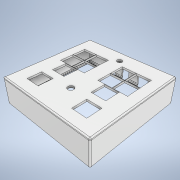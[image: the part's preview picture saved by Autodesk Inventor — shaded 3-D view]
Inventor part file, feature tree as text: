
AUTODESK INVENTOR PART (.ipt)
format: ipt  version: 2022.3 (Build 263350000, 350)  size: 703,488 bytes
history: native  units: mm
features: reference x13, other x6, extrude x4, fillet x3, pattern_circular x1, projected_geometry x1
ambient origin geometry x8: Origin, YZ Plane, XZ Plane, XY Plane, X Axis, Y Axis, Z Axis, Center Point
bodies: Body1 (feature_tree)
feature tree (28):
  other  "Lid"
  other  "Top_face_sketch"
  extrude  "Lid_face"  Depth=130.0mm
  extrude  "Walls"  Depth=130.0mm
  other  "Profile_sketch"
  extrude  "Wall_groove"  Depth=2.0mm
  fillet  "Bottom_fillet"  Radius=2.5mm
  pattern_circular  "Wall_groove_symmetry"  [2 undecoded]
  fillet  "Groove_fillets"  Radius=1.0mm
  extrude  "Cable cutouts"  Depth=2.0mm
  fillet  "Outer_edge_fillets"  Radius=2.0mm
  projected_geometry  "Projected Loop1"
  reference  "Reference1"
  reference  "Reference2"
  reference  "Reference3"
  reference  "Reference4"
  reference  "Reference5"
  reference  "Reference6"
  reference  "Reference7"
  reference  "Reference8"
  reference  "Reference9"
  reference  "Reference10"
  reference  "Reference11"
  reference  "Reference12"
  reference  "Reference13"
  other  "<userpath>\Dropbox (Personal)\SuperSTEM\FIB\FIBcontroller\Enclosure\Enclosure_with_PCB.iam"
  other  "Enclosure_with_PCB.iam"
  other  "FIBcontroller:1"
note: 2 required parameter values undecoded (feature->parameter linkage not recoverable at this tier; creation-order binding heuristic only, values carry confidence <= 0.55)
